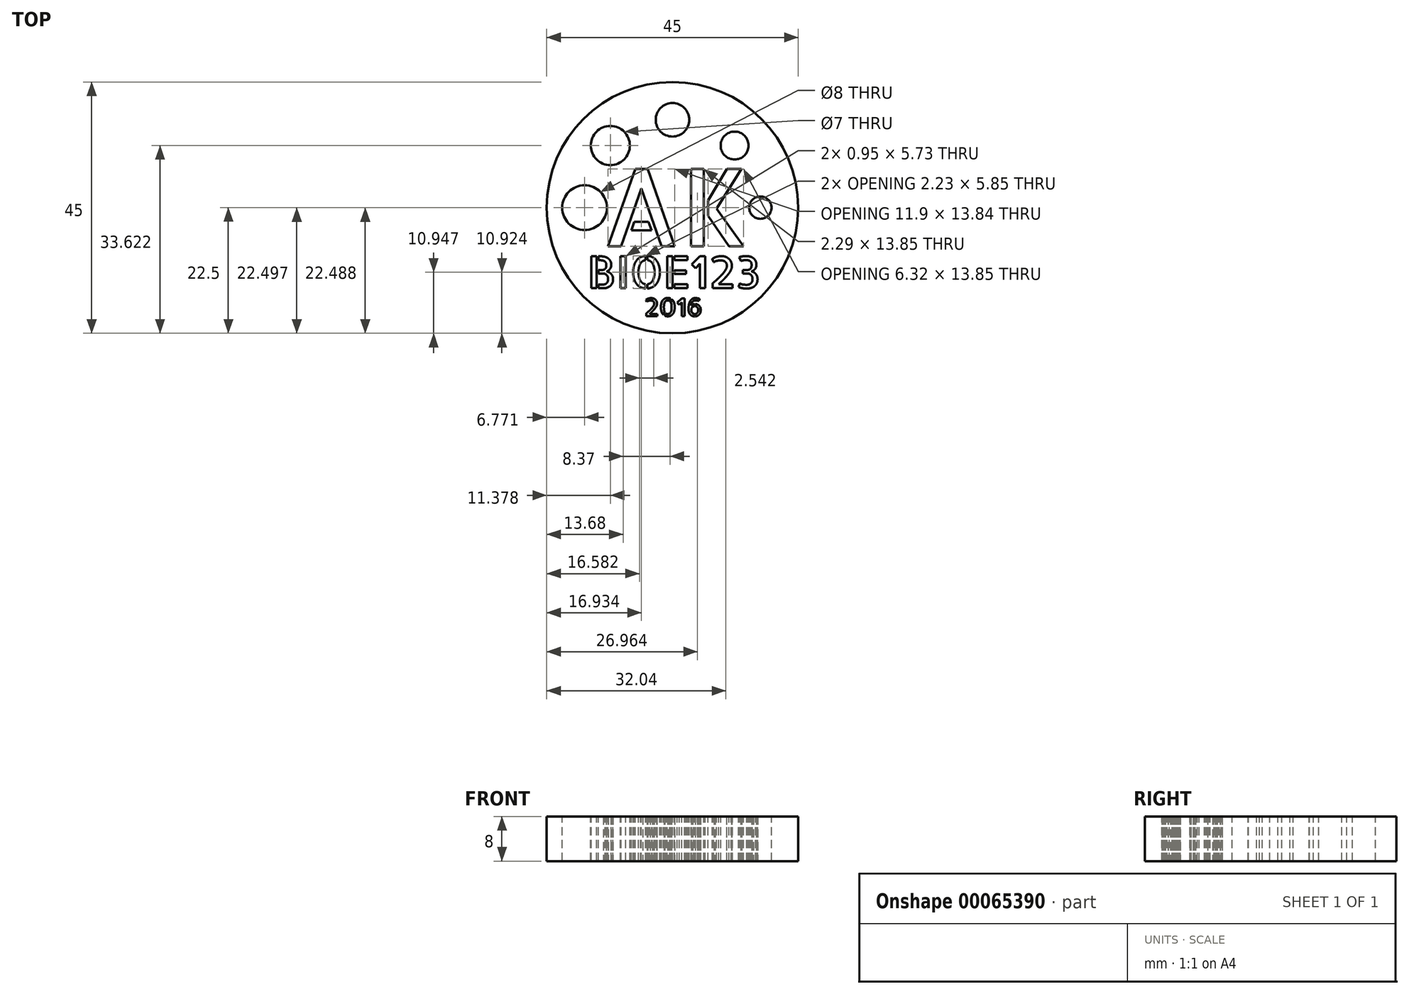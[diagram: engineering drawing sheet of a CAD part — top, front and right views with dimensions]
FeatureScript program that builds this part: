
annotation { "Feature Type Name" : "Feature", "Feature Type Description" : "" }
export const myFeature = defineFeature(function(context is Context, id is Id, definition is map)
    precondition{}
    {
        {
            var Q0;
            Q0=qCreatedBy(makeId("Top.planeOp"),FACE);
            var sketch = newSketch(context, id + "F0", { "sketchPlane" : qUnion([Q0])});
            skCircle(sketch, "E0", {"center": v(0, 0) * mm, "radius": 22.5 * mm});
            skSolve(sketch);
        }
        {
            var Q0;
            Q0=makeQuery(id+"F0.imprint","IMPRINT",FACE,{"disambiguationData":[TD([[makeQuery(id+"F0.imprint","IMPRINT",EDGE,{"derivedFrom":sQuery(id+"F0.wireOp",EDGE,"E0")}),1.0]])]});
            extrude(context, id + "F1", {"entities" : qUnion([Q0]), "depth" : 8 * mm});
        }
        {
            var Q0;
            Q0=makeQuery(id+"F1.opExtrude","CAP_FACE",FACE,{"disambiguationData":[OSD([sQuery(id+"F0.wireOp",EDGE,"E0")])],"isStart":false});
            cPlane(context, id + "F2", {"entities" : qUnion([Q0]), "cplaneType" : CPlaneType.OFFSET, "offset" : 0 * mm, "width" : 152.4 * mm, "height" : 152.4 * mm});
        }
        {
            var Q0;
            Q0=qCreatedBy(id+"F2.planeOp",FACE);
            var sketch = newSketch(context, id + "F3", { "sketchPlane" : qUnion([Q0])});
            skCircle(sketch, "E1", {"center": v(0, 0) * mm, "radius": 22.5 * mm});
            skText(sketch, "E2", { "text": "BIOE123", "fontName": "AllertaStencil-Regular.ttf"});
            skText(sketch, "E3", { "text": "2016", "fontName": "AllertaStencil-Regular.ttf"});
            skText(sketch, "E4", { "text": "AK", "fontName": "AllertaStencil-Regular.ttf"});
            skLineSegment(sketch, "E5", {"start": v(12.7, 6.93) * mm, "end": v(22.5, 0) * mm, "construction": true});
            skLineSegment(sketch, "E6", {"start": v(22.5, 0) * mm, "end": v(12.7, -6.93) * mm, "construction": true});
            skLineSegment(sketch, "E7", {"start": v(-12.7, -6.93) * mm, "end": v(-22.5, 0) * mm, "construction": true});
            skLineSegment(sketch, "E8", {"start": v(-22.5, 0) * mm, "end": v(-12.7, 6.93) * mm, "construction": true});
            skCircle(sketch, "E9", {"center": v(0, 0) * mm, "radius": 15.73 * mm, "construction": true});
            skLineSegment(sketch, "E10", {"start": v(0, 0) * mm, "end": v(-15.73, 0) * mm, "construction": true});
            skLineSegment(sketch, "E11", {"start": v(0, 0) * mm, "end": v(15.73, 0) * mm, "construction": true});
            skPoint(sketch, "E11.endSnap0", {"position": v(12.7, 0) * mm});
            skLineSegment(sketch, "E12", {"start": v(0, 0) * mm, "end": v(0, 15.73) * mm, "construction": true});
            skLineSegment(sketch, "E13", {"start": v(0, 0) * mm, "end": v(11.12, 11.12) * mm, "construction": true});
            skLineSegment(sketch, "E14", {"start": v(0, 0) * mm, "end": v(-11.12, 11.12) * mm, "construction": true});
            skLineSegment(sketch, "E15", {"start": v(-11.12, 11.12) * mm, "end": v(0, 15.73) * mm, "construction": true});
            skLineSegment(sketch, "E16", {"start": v(11.12, 11.12) * mm, "end": v(0, 15.73) * mm, "construction": true});
            skLineSegment(sketch, "E17", {"start": v(-11.12, 11.12) * mm, "end": v(-15.73, 0) * mm, "construction": true});
            skLineSegment(sketch, "E18", {"start": v(11.12, 11.12) * mm, "end": v(15.73, 0) * mm, "construction": true});
            skCircle(sketch, "E19", {"center": v(-15.73, 0) * mm, "radius": 4 * mm});
            skCircle(sketch, "E20", {"center": v(-11.12, 11.12) * mm, "radius": 3.5 * mm});
            skCircle(sketch, "E21", {"center": v(0, 15.73) * mm, "radius": 3 * mm});
            skCircle(sketch, "E22", {"center": v(11.12, 11.12) * mm, "radius": 2.5 * mm});
            skCircle(sketch, "E23", {"center": v(15.73, 0) * mm, "radius": 2 * mm});
            const initialGuessF3  = {"E2": [-0.01524, -0.01444, 1, 0, 0.00573], "E3": [-0.00508, -0.01944, 1, 0, 0.00322], "E4": [-0.0127, -0.00693, 1, 0, 0.01386]};
            skSetInitialGuess(sketch, initialGuessF3);
            skSolve(sketch);
        }
        {
            var Q0;
            Q0=makeQuery(id+"F3.imprint","IMPRINT",FACE,{"disambiguationData":[TD([[makeQuery(id+"F3.imprint","IMPRINT",EDGE,{"derivedFrom":sQuery(id+"F3.wireOp",EDGE,"E2.sketch_text.stroke-39")}),-1.0]])]});
            var Q1;
            Q1=makeQuery(id+"F3.imprint","IMPRINT",FACE,{"disambiguationData":[TD([[makeQuery(id+"F3.imprint","IMPRINT",EDGE,{"derivedFrom":sQuery(id+"F3.wireOp",EDGE,"E2.sketch_text.stroke-0")}),-1.0]])]});
            var Q2;
            Q2=makeQuery(id+"F3.imprint","IMPRINT",FACE,{"disambiguationData":[TD([[makeQuery(id+"F3.imprint","IMPRINT",EDGE,{"derivedFrom":sQuery(id+"F3.wireOp",EDGE,"E2.sketch_text.stroke-43")}),-1.0]])]});
            var Q3;
            Q3=makeQuery(id+"F3.imprint","IMPRINT",FACE,{"disambiguationData":[TD([[makeQuery(id+"F3.imprint","IMPRINT",EDGE,{"derivedFrom":sQuery(id+"F3.wireOp",EDGE,"E2.sketch_text.stroke-47")}),-1.0]])]});
            var Q4;
            Q4=makeQuery(id+"F3.imprint","IMPRINT",FACE,{"disambiguationData":[TD([[makeQuery(id+"F3.imprint","IMPRINT",EDGE,{"derivedFrom":sQuery(id+"F3.wireOp",EDGE,"E2.sketch_text.stroke-65")}),-1.0]])]});
            var Q5;
            Q5=makeQuery(id+"F3.imprint","IMPRINT",FACE,{"disambiguationData":[TD([[makeQuery(id+"F3.imprint","IMPRINT",EDGE,{"derivedFrom":sQuery(id+"F3.wireOp",EDGE,"E2.sketch_text.stroke-83")}),-1.0]])]});
            var Q6;
            Q6=makeQuery(id+"F3.imprint","IMPRINT",FACE,{"disambiguationData":[TD([[makeQuery(id+"F3.imprint","IMPRINT",EDGE,{"derivedFrom":sQuery(id+"F3.wireOp",EDGE,"E2.sketch_text.stroke-87")}),-1.0]])]});
            var Q7;
            Q7=makeQuery(id+"F3.imprint","IMPRINT",FACE,{"disambiguationData":[TD([[makeQuery(id+"F3.imprint","IMPRINT",EDGE,{"derivedFrom":sQuery(id+"F3.wireOp",EDGE,"E2.sketch_text.stroke-95")}),-1.0]])]});
            var Q8;
            Q8=makeQuery(id+"F3.imprint","IMPRINT",FACE,{"disambiguationData":[TD([[makeQuery(id+"F3.imprint","IMPRINT",EDGE,{"derivedFrom":sQuery(id+"F3.wireOp",EDGE,"E2.sketch_text.stroke-91")}),-1.0]])]});
            var Q9;
            Q9=makeQuery(id+"F3.imprint","IMPRINT",FACE,{"disambiguationData":[TD([[makeQuery(id+"F3.imprint","IMPRINT",EDGE,{"derivedFrom":sQuery(id+"F3.wireOp",EDGE,"E2.sketch_text.stroke-99")}),-1.0]])]});
            var Q10;
            Q10=makeQuery(id+"F3.imprint","IMPRINT",FACE,{"disambiguationData":[TD([[makeQuery(id+"F3.imprint","IMPRINT",EDGE,{"derivedFrom":sQuery(id+"F3.wireOp",EDGE,"E2.sketch_text.stroke-106")}),-1.0]])]});
            var Q11;
            Q11=makeQuery(id+"F3.imprint","IMPRINT",FACE,{"disambiguationData":[TD([[makeQuery(id+"F3.imprint","IMPRINT",EDGE,{"derivedFrom":sQuery(id+"F3.wireOp",EDGE,"E2.sketch_text.stroke-139")}),-1.0]])]});
            var Q12;
            Q12=makeQuery(id+"F3.imprint","IMPRINT",FACE,{"disambiguationData":[TD([[makeQuery(id+"F3.imprint","IMPRINT",EDGE,{"derivedFrom":sQuery(id+"F3.wireOp",EDGE,"E3.sketch_text.stroke-104")}),-1.0]])]});
            var Q13;
            Q13=makeQuery(id+"F3.imprint","IMPRINT",FACE,{"disambiguationData":[TD([[makeQuery(id+"F3.imprint","IMPRINT",EDGE,{"derivedFrom":sQuery(id+"F3.wireOp",EDGE,"E3.sketch_text.stroke-73")}),-1.0]])]});
            var Q14;
            Q14=makeQuery(id+"F3.imprint","IMPRINT",FACE,{"disambiguationData":[TD([[makeQuery(id+"F3.imprint","IMPRINT",EDGE,{"derivedFrom":sQuery(id+"F3.wireOp",EDGE,"E3.sketch_text.stroke-66")}),-1.0]])]});
            var Q15;
            Q15=makeQuery(id+"F3.imprint","IMPRINT",FACE,{"disambiguationData":[TD([[makeQuery(id+"F3.imprint","IMPRINT",EDGE,{"derivedFrom":sQuery(id+"F3.wireOp",EDGE,"E3.sketch_text.stroke-49")}),-1.0]])]});
            var Q16;
            Q16=makeQuery(id+"F3.imprint","IMPRINT",FACE,{"disambiguationData":[TD([[makeQuery(id+"F3.imprint","IMPRINT",EDGE,{"derivedFrom":sQuery(id+"F3.wireOp",EDGE,"E3.sketch_text.stroke-33")}),-1.0]])]});
            var Q17;
            Q17=makeQuery(id+"F3.imprint","IMPRINT",FACE,{"disambiguationData":[TD([[makeQuery(id+"F3.imprint","IMPRINT",EDGE,{"derivedFrom":sQuery(id+"F3.wireOp",EDGE,"E3.sketch_text.stroke-0")}),-1.0]])]});
            extrude(context, id + "F4", {"entities" : qUnion([Q0, Q1, Q2, Q3, Q4, Q5, Q6, Q7, Q8, Q9, Q10, Q11, Q12, Q13, Q14, Q15, Q16, Q17]), "operationType" : NewBodyOperationType.REMOVE, "oppositeDirection" : true, "depth" : 8 * mm});
        }
        {
            var Q0;
            Q0=makeQuery(id+"F3.imprint","IMPRINT",FACE,{"disambiguationData":[TD([[makeQuery(id+"F3.imprint","IMPRINT",EDGE,{"derivedFrom":sQuery(id+"F3.wireOp",EDGE,"E4.sketch_text.stroke-0")}),-1.0]])]});
            var Q1;
            Q1=makeQuery(id+"F3.imprint","IMPRINT",FACE,{"disambiguationData":[TD([[makeQuery(id+"F3.imprint","IMPRINT",EDGE,{"derivedFrom":sQuery(id+"F3.wireOp",EDGE,"E4.sketch_text.stroke-7")}),-1.0]])]});
            var Q2;
            Q2=makeQuery(id+"F3.imprint","IMPRINT",FACE,{"disambiguationData":[TD([[makeQuery(id+"F3.imprint","IMPRINT",EDGE,{"derivedFrom":sQuery(id+"F3.wireOp",EDGE,"E4.sketch_text.stroke-11")}),-1.0]])]});
            var Q3;
            Q3=makeQuery(id+"F3.imprint","IMPRINT",FACE,{"disambiguationData":[TD([[makeQuery(id+"F3.imprint","IMPRINT",EDGE,{"derivedFrom":sQuery(id+"F3.wireOp",EDGE,"E4.sketch_text.stroke-15")}),-1.0]])]});
            extrude(context, id + "F5", {"entities" : qUnion([Q0, Q1, Q2, Q3]), "operationType" : NewBodyOperationType.REMOVE, "oppositeDirection" : true, "depth" : 8 * mm});
        }
        {
            var Q0;
            Q0=makeQuery(id+"F3.imprint","IMPRINT",FACE,{"disambiguationData":[TD([[makeQuery(id+"F3.imprint","IMPRINT",EDGE,{"derivedFrom":sQuery(id+"F3.wireOp",EDGE,"E19")}),1.0]])]});
            var Q1;
            Q1=makeQuery(id+"F3.imprint","IMPRINT",FACE,{"disambiguationData":[TD([[makeQuery(id+"F3.imprint","IMPRINT",EDGE,{"derivedFrom":sQuery(id+"F3.wireOp",EDGE,"E20")}),1.0]])]});
            var Q2;
            Q2=makeQuery(id+"F3.imprint","IMPRINT",FACE,{"disambiguationData":[TD([[makeQuery(id+"F3.imprint","IMPRINT",EDGE,{"derivedFrom":sQuery(id+"F3.wireOp",EDGE,"E21")}),1.0]])]});
            var Q3;
            Q3=makeQuery(id+"F3.imprint","IMPRINT",FACE,{"disambiguationData":[TD([[makeQuery(id+"F3.imprint","IMPRINT",EDGE,{"derivedFrom":sQuery(id+"F3.wireOp",EDGE,"E22")}),1.0]])]});
            var Q4;
            Q4=makeQuery(id+"F3.imprint","IMPRINT",FACE,{"disambiguationData":[TD([[makeQuery(id+"F3.imprint","IMPRINT",EDGE,{"derivedFrom":sQuery(id+"F3.wireOp",EDGE,"E23")}),1.0]])]});
            extrude(context, id + "F6", {"entities" : qUnion([Q0, Q1, Q2, Q3, Q4]), "operationType" : NewBodyOperationType.REMOVE, "oppositeDirection" : true, "depth" : 8 * mm});
        }
    });
